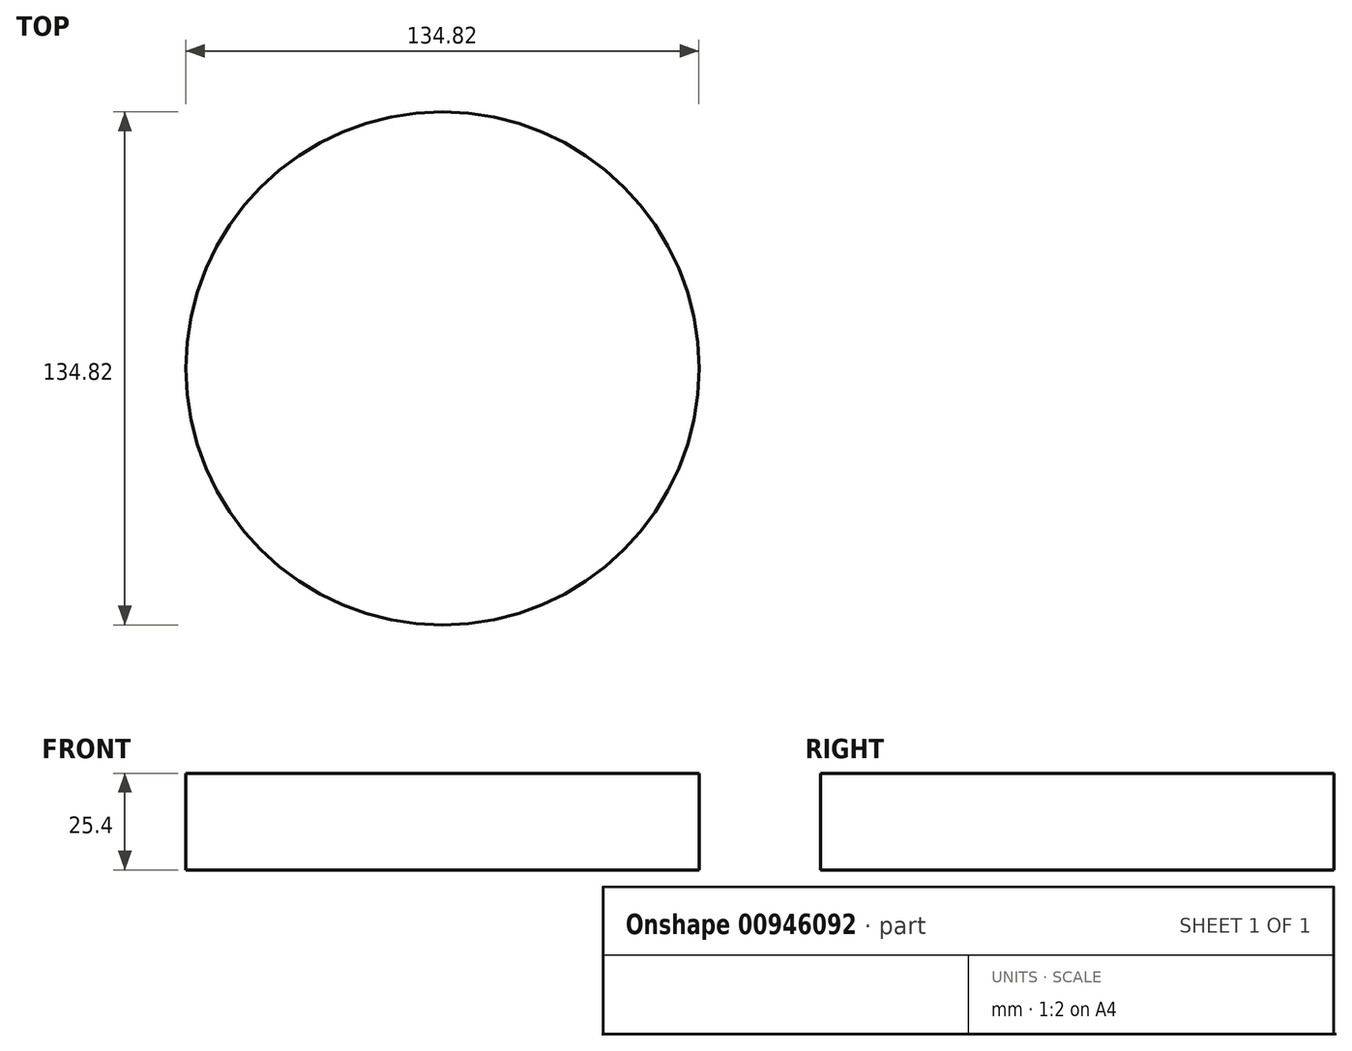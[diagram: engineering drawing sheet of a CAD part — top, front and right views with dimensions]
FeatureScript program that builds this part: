
annotation { "Feature Type Name" : "Feature", "Feature Type Description" : "" }
export const myFeature = defineFeature(function(context is Context, id is Id, definition is map)
    precondition{}
    {
        {
            var Q0;
            Q0=qCreatedBy(makeId("Top.planeOp"),FACE);
            var sketch = newSketch(context, id + "F0", { "sketchPlane" : qUnion([Q0])});
            skCircle(sketch, "E0", {"center": v(0, 0) * mm, "radius": 67.41 * mm});
            skSolve(sketch);
        }
        {
            var Q0;
            Q0 = qSketchRegion(id + "F0", true);
            extrude(context, id + "F1", {"entities" : qUnion([Q0]), "depth" : 25.4 * mm, "offsetDistance" : 25.4 * mm});
        }
    });
